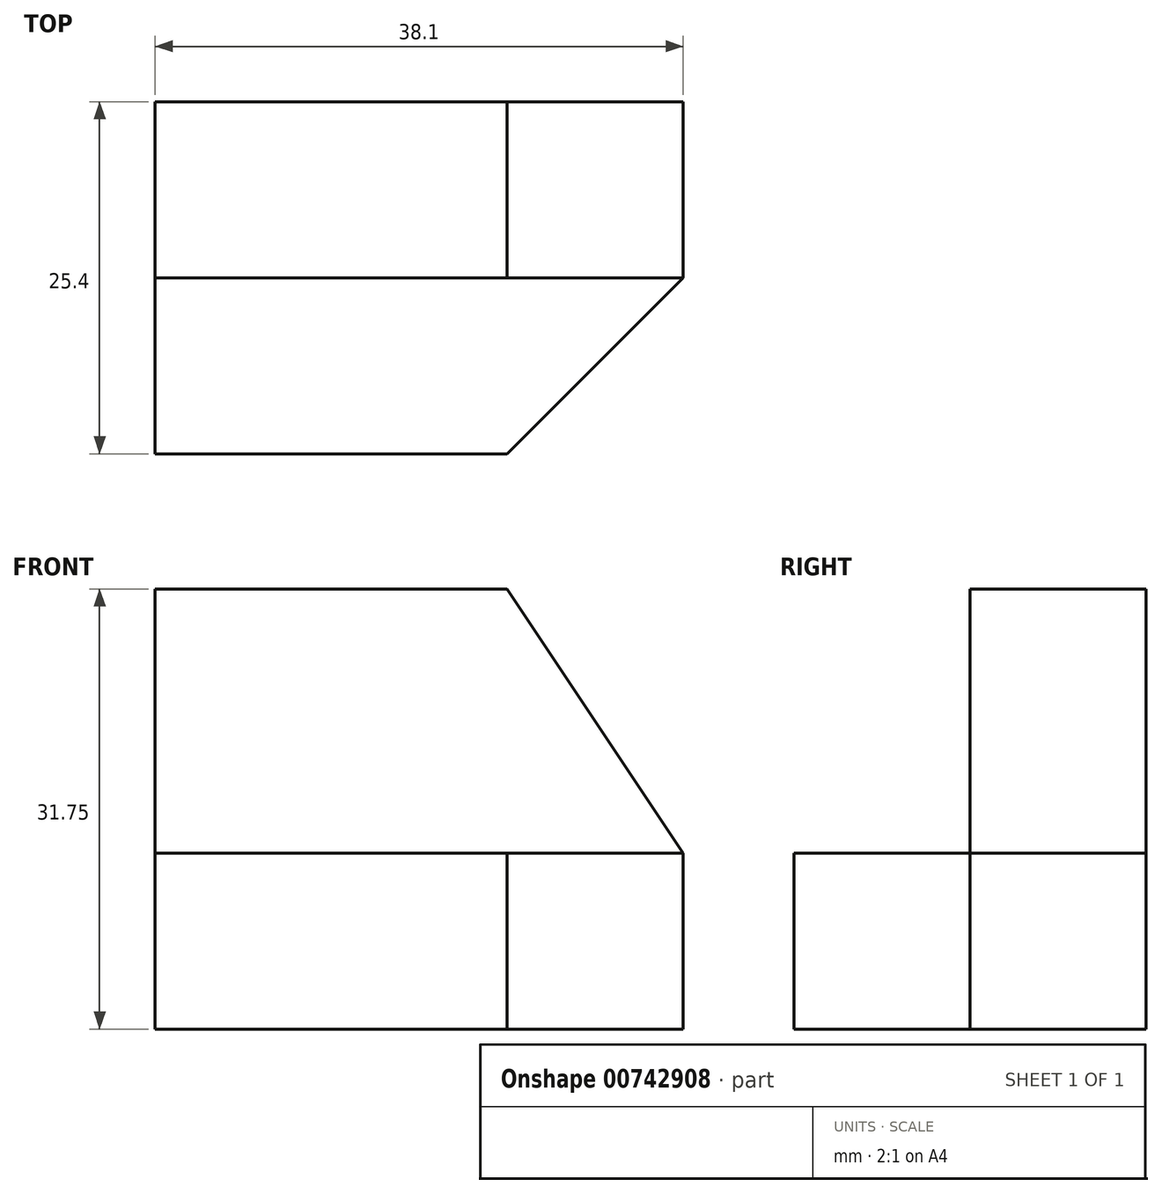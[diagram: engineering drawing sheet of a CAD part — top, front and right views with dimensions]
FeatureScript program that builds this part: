
annotation { "Feature Type Name" : "Feature", "Feature Type Description" : "" }
export const myFeature = defineFeature(function(context is Context, id is Id, definition is map)
    precondition{}
    {
        {
            var Q0;
            Q0=qCreatedBy(makeId("Front.planeOp"),FACE);
            var sketch = newSketch(context, id + "F0", { "sketchPlane" : qUnion([Q0])});
            skLineSegment(sketch, "E0", {"start": v(0, 0) * mm, "end": v(38.1, 0) * mm});
            skLineSegment(sketch, "E1", {"start": v(38.1, 0) * mm, "end": v(38.1, 12.7) * mm});
            skLineSegment(sketch, "E2", {"start": v(38.1, 12.7) * mm, "end": v(0, 12.7) * mm});
            skLineSegment(sketch, "E3", {"start": v(0, 12.7) * mm, "end": v(0, 0) * mm});
            skSolve(sketch);
        }
        {
            var Q0;
            Q0=makeQuery(id+"F0.imprint","IMPRINT",FACE,{"disambiguationData":[TD([[makeQuery(id+"F0.imprint","IMPRINT",EDGE,{"derivedFrom":sQuery(id+"F0.wireOp",EDGE,"E0")}),1.0]])]});
            extrude(context, id + "F1", {"entities" : qUnion([Q0]), "oppositeDirection" : true, "depth" : 25.4 * mm, "offsetDistance" : 25.4 * mm});
        }
        {
            var Q0;
            Q0=makeQuery(id+"F1.opExtrude","SWEPT_FACE",FACE,{"disambiguationData":[OSD([sQuery(id+"F0.wireOp",EDGE,"E2")])]});
            var sketch = newSketch(context, id + "F2", { "sketchPlane" : qUnion([Q0])});
            skLineSegment(sketch, "E4", {"start": v(25.4, 0) * mm, "end": v(38.1, 12.7) * mm});
            skLineSegment(sketch, "E5", {"start": v(38.1, 12.7) * mm, "end": v(38.1, 0) * mm});
            skLineSegment(sketch, "E6", {"start": v(38.1, 0) * mm, "end": v(25.4, 0) * mm});
            skSolve(sketch);
        }
        {
            var Q0;
            Q0=makeQuery(id+"F2.imprint","IMPRINT",FACE,{"disambiguationData":[TD([[makeQuery(id+"F2.imprint","IMPRINT",EDGE,{"derivedFrom":sQuery(id+"F2.wireOp",EDGE,"E4")}),-1.0]])]});
            extrude(context, id + "F3", {"entities" : qUnion([Q0]), "operationType" : NewBodyOperationType.REMOVE, "oppositeDirection" : true, "depth" : 25.4 * mm, "offsetDistance" : 25.4 * mm});
        }
        {
            var Q0;
            Q0=makeQuery(id+"F1.opExtrude","SWEPT_FACE",FACE,{"disambiguationData":[OSD([sQuery(id+"F0.wireOp",EDGE,"E2")])]});
            var sketch = newSketch(context, id + "F4", { "sketchPlane" : qUnion([Q0])});
            skLineSegment(sketch, "E7", {"start": v(38.1, 12.7) * mm, "end": v(0, 12.7) * mm});
            skLineSegment(sketch, "E8", {"start": v(0, 12.7) * mm, "end": v(0, 25.4) * mm});
            skLineSegment(sketch, "E9", {"start": v(0, 25.4) * mm, "end": v(38.1, 25.4) * mm});
            skLineSegment(sketch, "E10", {"start": v(38.1, 25.4) * mm, "end": v(38.1, 12.7) * mm});
            skSolve(sketch);
        }
        {
            var Q0;
            Q0=makeQuery(id+"F4.imprint","IMPRINT",FACE,{"disambiguationData":[TD([[makeQuery(id+"F4.imprint","IMPRINT",EDGE,{"derivedFrom":sQuery(id+"F4.wireOp",EDGE,"E7")}),-1.0]])]});
            extrude(context, id + "F5", {"entities" : qUnion([Q0]), "operationType" : NewBodyOperationType.ADD, "depth" : 19.05 * mm, "offsetDistance" : 25.4 * mm});
        }
        {
            var Q0;
            Q0=makeQuery(id+"F5.opExtrude","SWEPT_FACE",FACE,{"disambiguationData":[OSD([sQuery(id+"F4.wireOp",EDGE,"E7")])]});
            var sketch = newSketch(context, id + "F6", { "sketchPlane" : qUnion([Q0])});
            skLineSegment(sketch, "E11", {"start": v(38.1, 12.7) * mm, "end": v(25.4, 31.75) * mm});
            skLineSegment(sketch, "E12", {"start": v(25.4, 31.75) * mm, "end": v(38.1, 31.75) * mm});
            skLineSegment(sketch, "E13", {"start": v(38.1, 31.75) * mm, "end": v(38.1, 12.7) * mm});
            skSolve(sketch);
        }
        {
            var Q0;
            Q0=makeQuery(id+"F6.imprint","IMPRINT",FACE,{"disambiguationData":[TD([[makeQuery(id+"F6.imprint","IMPRINT",EDGE,{"derivedFrom":sQuery(id+"F6.wireOp",EDGE,"E11")}),-1.0]])]});
            extrude(context, id + "F7", {"entities" : qUnion([Q0]), "operationType" : NewBodyOperationType.REMOVE, "oppositeDirection" : true, "depth" : 25.4 * mm, "offsetDistance" : 25.4 * mm});
        }
    });
